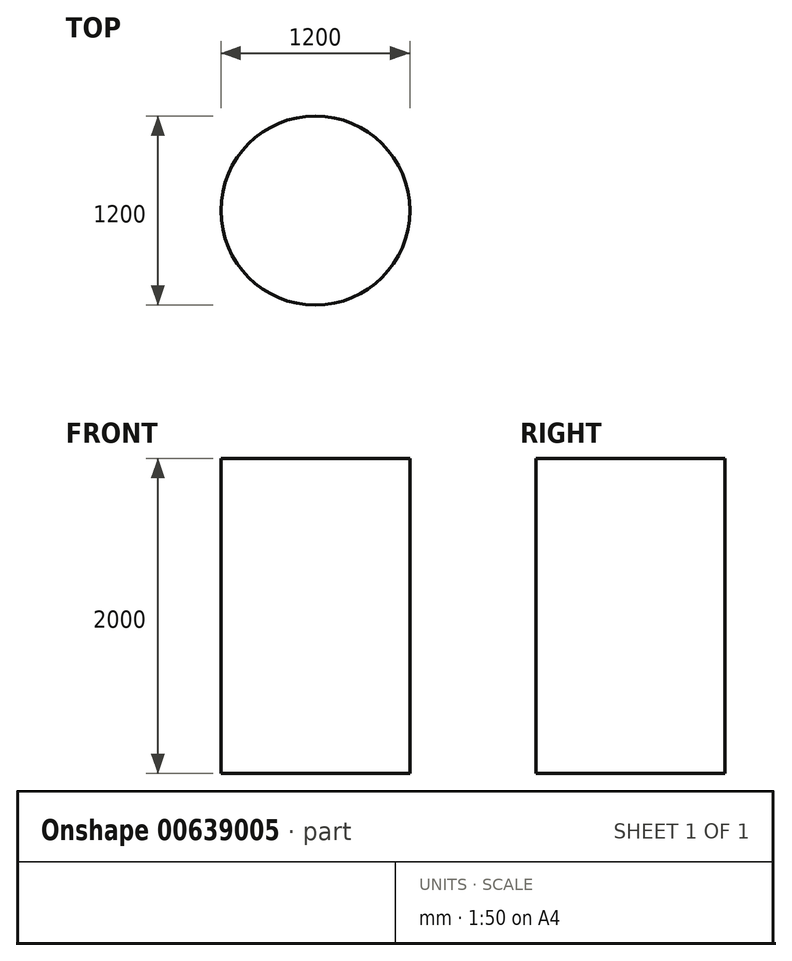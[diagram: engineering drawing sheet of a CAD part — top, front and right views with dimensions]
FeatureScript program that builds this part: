
annotation { "Feature Type Name" : "Feature", "Feature Type Description" : "" }
export const myFeature = defineFeature(function(context is Context, id is Id, definition is map)
    precondition{}
    {
        {
            var Q0;
            Q0=qCreatedBy(makeId("Top.planeOp"),FACE);
            var sketch = newSketch(context, id + "F0", { "sketchPlane" : qUnion([Q0])});
            skCircle(sketch, "E0", {"center": v(0, 0) * mm, "radius": 600 * mm});
            skSolve(sketch);
        }
        {
            var Q0;
            Q0 = qSketchRegion(id + "F0", true);
            extrude(context, id + "F1", {"entities" : qUnion([Q0]), "depth" : 2000 * mm, "offsetDistance" : 25 * mm});
        }
    });
